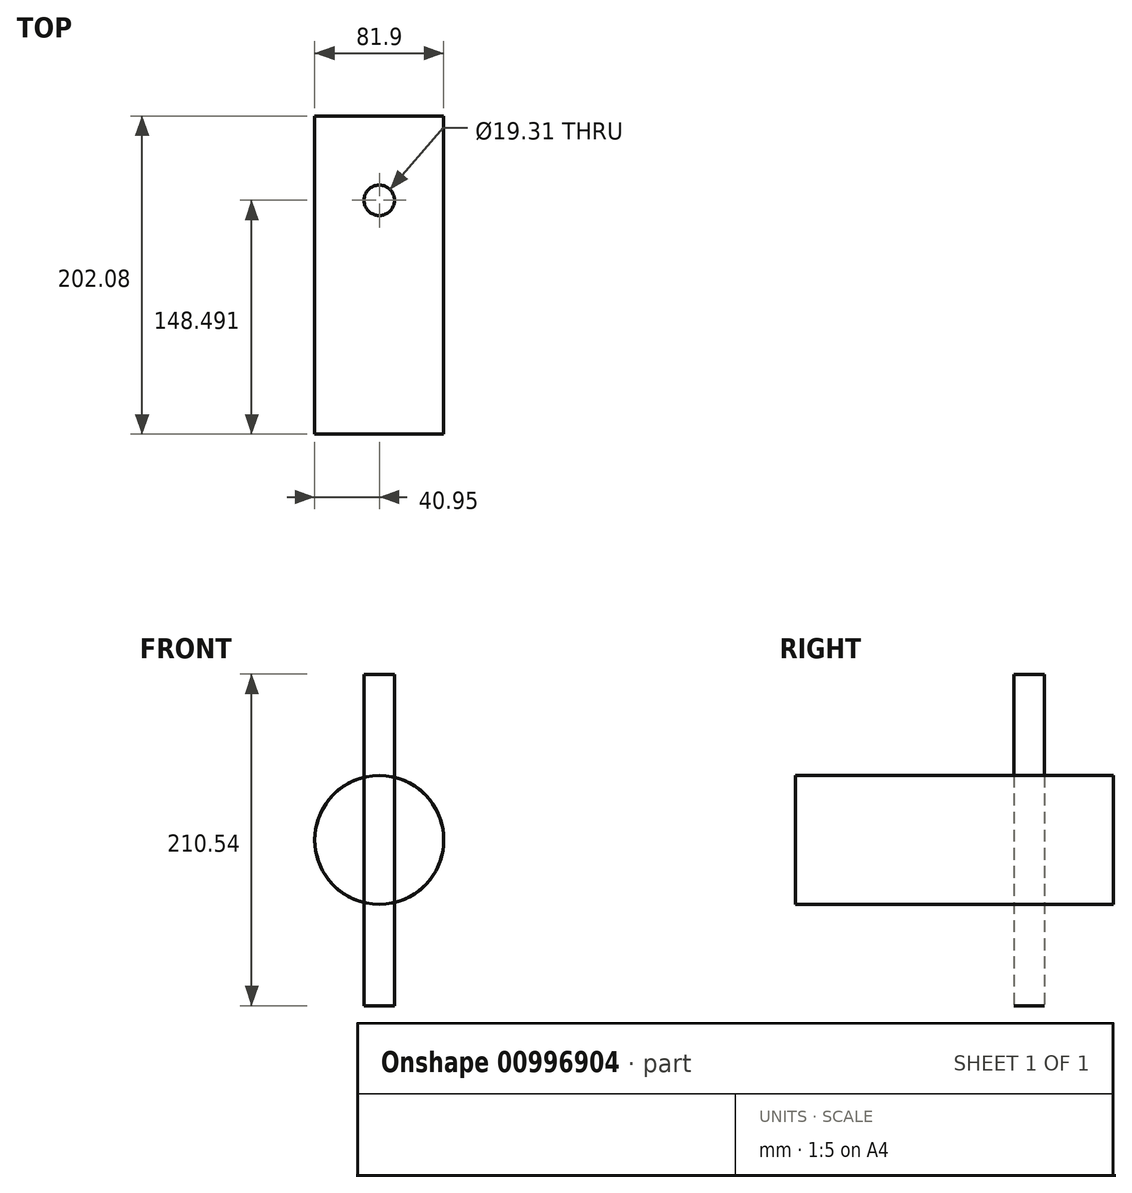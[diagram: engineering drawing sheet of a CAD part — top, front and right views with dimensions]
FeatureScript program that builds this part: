
annotation { "Feature Type Name" : "Feature", "Feature Type Description" : "" }
export const myFeature = defineFeature(function(context is Context, id is Id, definition is map)
    precondition{}
    {
        {
            var Q0;
            Q0=qCreatedBy(makeId("Front.planeOp"),FACE);
            var sketch = newSketch(context, id + "F0", { "sketchPlane" : qUnion([Q0])});
            skCircle(sketch, "E0", {"center": v(0, 0) * mm, "radius": 40.95 * mm});
            skSolve(sketch);
        }
        {
            var Q0;
            Q0=sQuery(id+"F0.wireOp",EDGE,"E0");
            extrude(context, id + "F1", {"bodyType" : ToolBodyType.SURFACE, "surfaceEntities" : qUnion([Q0]), "depth" : 202.08 * mm, "offsetDistance" : 25.4 * mm});
        }
        {
            var Q0;
            Q0=qCreatedBy(makeId("Top.planeOp"),FACE);
            var sketch = newSketch(context, id + "F2", { "sketchPlane" : qUnion([Q0])});
            skCircle(sketch, "E1", {"center": v(0, -53.59) * mm, "radius": 9.66 * mm});
            skSolve(sketch);
        }
        {
            var Q0;
            Q0 = qSketchRegion(id + "F2", true);
            var Q1;
            Q1=sQuery(id+"F2.wireOp",EDGE,"E1");
            extrude(context, id + "F3", {"entities" : qUnion([Q0]), "bodyType" : ToolBodyType.SURFACE, "operationType" : NewBodyOperationType.REMOVE, "surfaceEntities" : qUnion([Q1]), "endBound" : BoundingType.SYMMETRIC, "oppositeDirection" : true, "depth" : 210.53 * mm, "offsetDistance" : 25.4 * mm});
        }
    });
